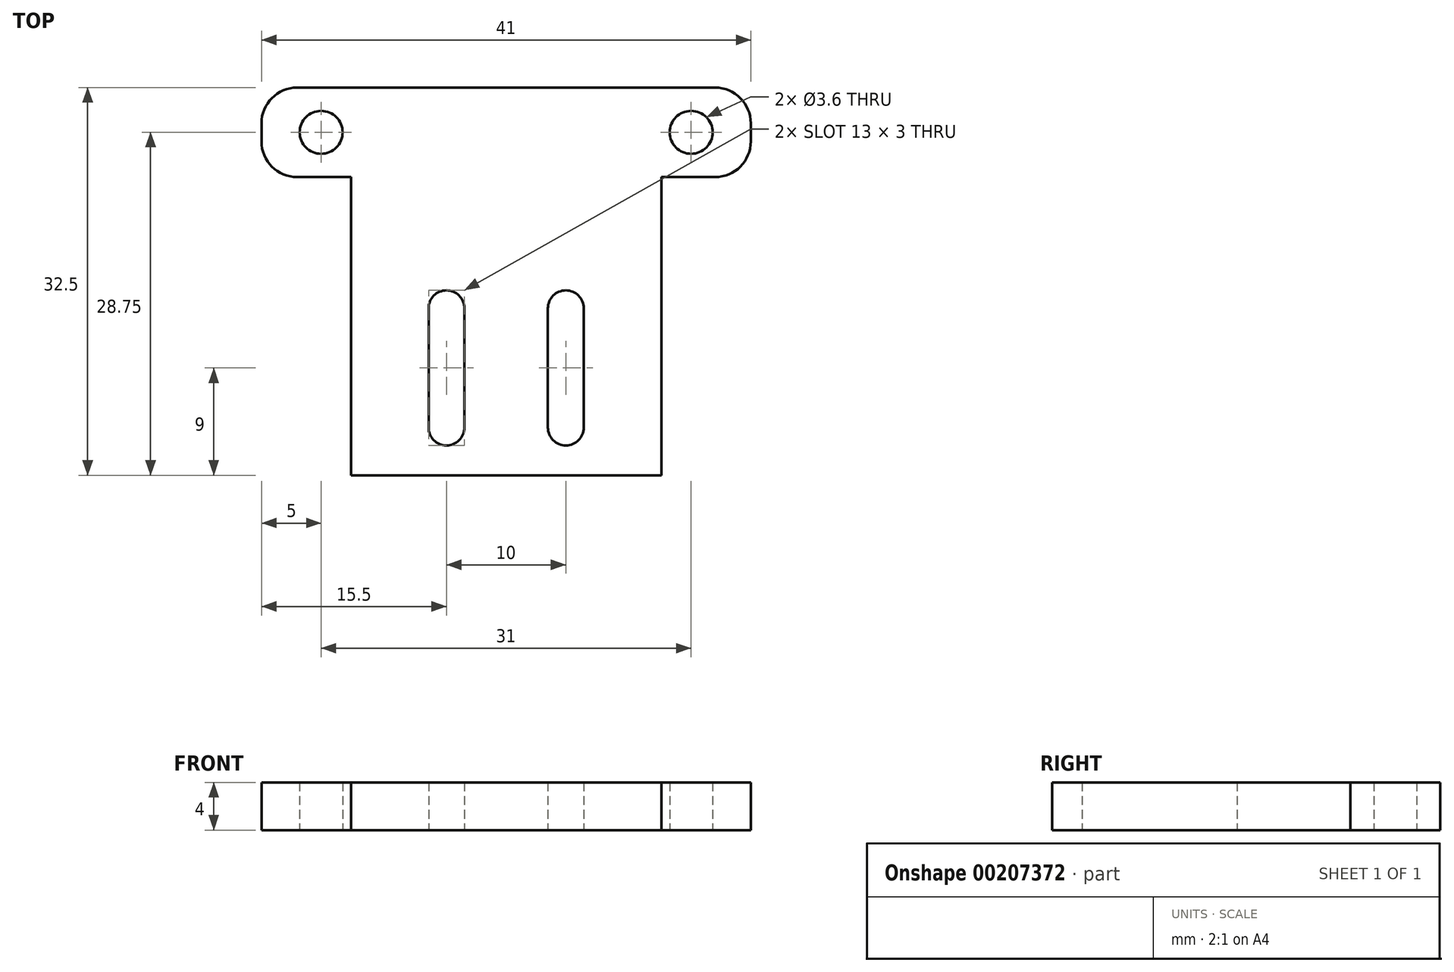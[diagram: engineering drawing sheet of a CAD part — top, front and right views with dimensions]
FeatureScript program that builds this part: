
annotation { "Feature Type Name" : "Feature", "Feature Type Description" : "" }
export const myFeature = defineFeature(function(context is Context, id is Id, definition is map)
    precondition{}
    {
        {
            var Q0;
            Q0=qCreatedBy(makeId("Top.planeOp"),FACE);
            var sketch = newSketch(context, id + "F0", { "sketchPlane" : qUnion([Q0])});
            skLineSegment(sketch, "E0.bottom", {"start": v(-41, 7.5) * mm, "end": v(0, 7.5) * mm});
            skLineSegment(sketch, "E0.top", {"start": v(-41, 0) * mm, "end": v(0, 0) * mm});
            skLineSegment(sketch, "E0.left", {"start": v(-41, 7.5) * mm, "end": v(-41, 0) * mm});
            skLineSegment(sketch, "E0.right", {"start": v(0, 7.5) * mm, "end": v(0, 0) * mm});
            skCircle(sketch, "E1", {"center": v(-36, 3.75) * mm, "radius": 1.8 * mm});
            skPoint(sketch, "E1.centerSnap0", {"position": v(-41, 3.75) * mm});
            skCircle(sketch, "E2", {"center": v(-5, 3.75) * mm, "radius": 1.8 * mm});
            skPoint(sketch, "E2.centerSnap0", {"position": v(0, 3.75) * mm});
            skLineSegment(sketch, "E3", {"start": v(-36, 3.75) * mm, "end": v(-5, 3.75) * mm, "construction": true});
            skPoint(sketch, "E4", {"position": v(-20.5, 7.5) * mm});
            skPoint(sketch, "E5", {"position": v(-20.5, 3.75) * mm});
            skLineSegment(sketch, "E6", {"start": v(-33.5, 0) * mm, "end": v(-33.5, -25) * mm});
            skLineSegment(sketch, "E7", {"start": v(-33.5, -25) * mm, "end": v(-7.5, -25) * mm});
            skLineSegment(sketch, "E8", {"start": v(-7.5, -25) * mm, "end": v(-7.5, 0) * mm});
            skPoint(sketch, "E9", {"position": v(-20.5, -25) * mm});
            skLineSegment(sketch, "E10", {"start": v(-27, -11) * mm, "end": v(-27, -21) * mm});
            skLineSegment(sketch, "E11", {"start": v(-24, -11) * mm, "end": v(-24, -21) * mm});
            skArc(sketch, "E12", {"start": v(-24, -11) * mm, "mid": v(-25.5, -9.5) * mm, "end": v(-27, -11) * mm});
            skArc(sketch, "E13", {"start": v(-27, -21) * mm, "mid": v(-25.5, -22.5) * mm, "end": v(-24, -21) * mm});
            skLineSegment(sketch, "E14", {"start": v(-20.5, 7.5) * mm, "end": v(-20.5, -25) * mm, "construction": true});
            skLineSegment(sketch, "E15.MirrorCS", {"start": v(-17, -11) * mm, "end": v(-17, -21) * mm});
            skLineSegment(sketch, "E16.MirrorCS", {"start": v(-14, -11) * mm, "end": v(-14, -21) * mm});
            skArc(sketch, "E17.MirrorCS", {"start": v(-17, -11) * mm, "mid": v(-15.5, -9.5) * mm, "end": v(-14, -11) * mm});
            skArc(sketch, "E18.MirrorCS", {"start": v(-14, -21) * mm, "mid": v(-15.5, -22.5) * mm, "end": v(-17, -21) * mm});
            skPoint(sketch, "E19", {"position": v(-30.5, -1.8) * mm});
            skPoint(sketch, "E20", {"position": v(-10.5, -1.8) * mm});
            skPoint(sketch, "E21", {"position": v(-10.5, -19.38) * mm});
            skPoint(sketch, "E22", {"position": v(-30.04, -19.38) * mm});
            skLineSegment(sketch, "E23", {"start": v(-30.5, -1.8) * mm, "end": v(-10.5, -1.8) * mm, "construction": true});
            skPoint(sketch, "E24", {"position": v(-20.5, -1.8) * mm});
            skSolve(sketch);
        }
        {
            var Q0;
            Q0=makeQuery(id+"F0.imprint","IMPRINT",FACE,{"disambiguationData":[TD([[makeQuery(id+"F0.imprint","IMPRINT",EDGE,{"derivedFrom":sQuery(id+"F0.wireOp",EDGE,"E0.bottom")}),-1.0]])]});
            var Q1;
            {var subQ5=sQuery(id+"F0.wireOp",EDGE,"QvUDmnyE-Zy62-BH61-VGX8-P0nBXhJbNSCf");Q1=makeQuery(id+"F0.imprint","IMPRINT",FACE,{"disambiguationData":[TD([[makeQuery(id+"F0.imprint","IMPRINT",EDGE,{"derivedFrom":subQ5}),1.0]])]});}
            var Q2;
            {var subQ0=sQuery(id+"F0.wireOp",EDGE,"E6");Q2=makeQuery(id+"F0.imprint","IMPRINT",FACE,{"disambiguationData":[TD([[makeQuery(id+"F0.imprint","IMPRINT",EDGE,{"derivedFrom":subQ0}),1.0]])]});}
            extrude(context, id + "F1", {"entities" : qUnion([Q0, Q1, Q2]), "offsetDistance" : 25 * mm, "depth" : 4 * mm});
        }
        {
            var Q0;
            Q0=makeQuery(id+"F1.opExtrude","SWEPT_EDGE",EDGE,{"disambiguationData":[OSD([sQuery(id+"F0.wireOp",EDGE,"E0.top"),sQuery(id+"F0.wireOp",EDGE,"E0.right")])]});
            var Q1;
            Q1=makeQuery(id+"F1.opExtrude","SWEPT_EDGE",EDGE,{"disambiguationData":[OSD([sQuery(id+"F0.wireOp",EDGE,"E0.bottom"),sQuery(id+"F0.wireOp",EDGE,"E0.right")])]});
            var Q2;
            Q2=makeQuery(id+"F1.opExtrude","SWEPT_EDGE",EDGE,{"disambiguationData":[OSD([sQuery(id+"F0.wireOp",EDGE,"E0.top"),sQuery(id+"F0.wireOp",EDGE,"E0.left")])]});
            var Q3;
            Q3=makeQuery(id+"F1.opExtrude","SWEPT_EDGE",EDGE,{"disambiguationData":[OSD([sQuery(id+"F0.wireOp",EDGE,"E0.bottom"),sQuery(id+"F0.wireOp",EDGE,"E0.left")])]});
            var Q4;
            Q4=makeQuery(id+"FaicOspiirSvBIv_1.opExtrude","CAP_EDGE",EDGE,{"disambiguationData":[OSD([sQuery(id+"F0.wireOp",EDGE,"E6")])],"isStart":false});
            var Q5;
            Q5=makeQuery(id+"FaicOspiirSvBIv_1.opExtrude","CAP_EDGE",EDGE,{"disambiguationData":[OSD([sQuery(id+"F0.wireOp",EDGE,"E8")])],"isStart":false});
            fillet(context, id + "F2", {"entities" : qUnion([Q0, Q1, Q2, Q3, Q4, Q5]), "radius" : 3 * mm, "tangentPropagation" : true, "allowEdgeOverflow" : false});
        }
    });
